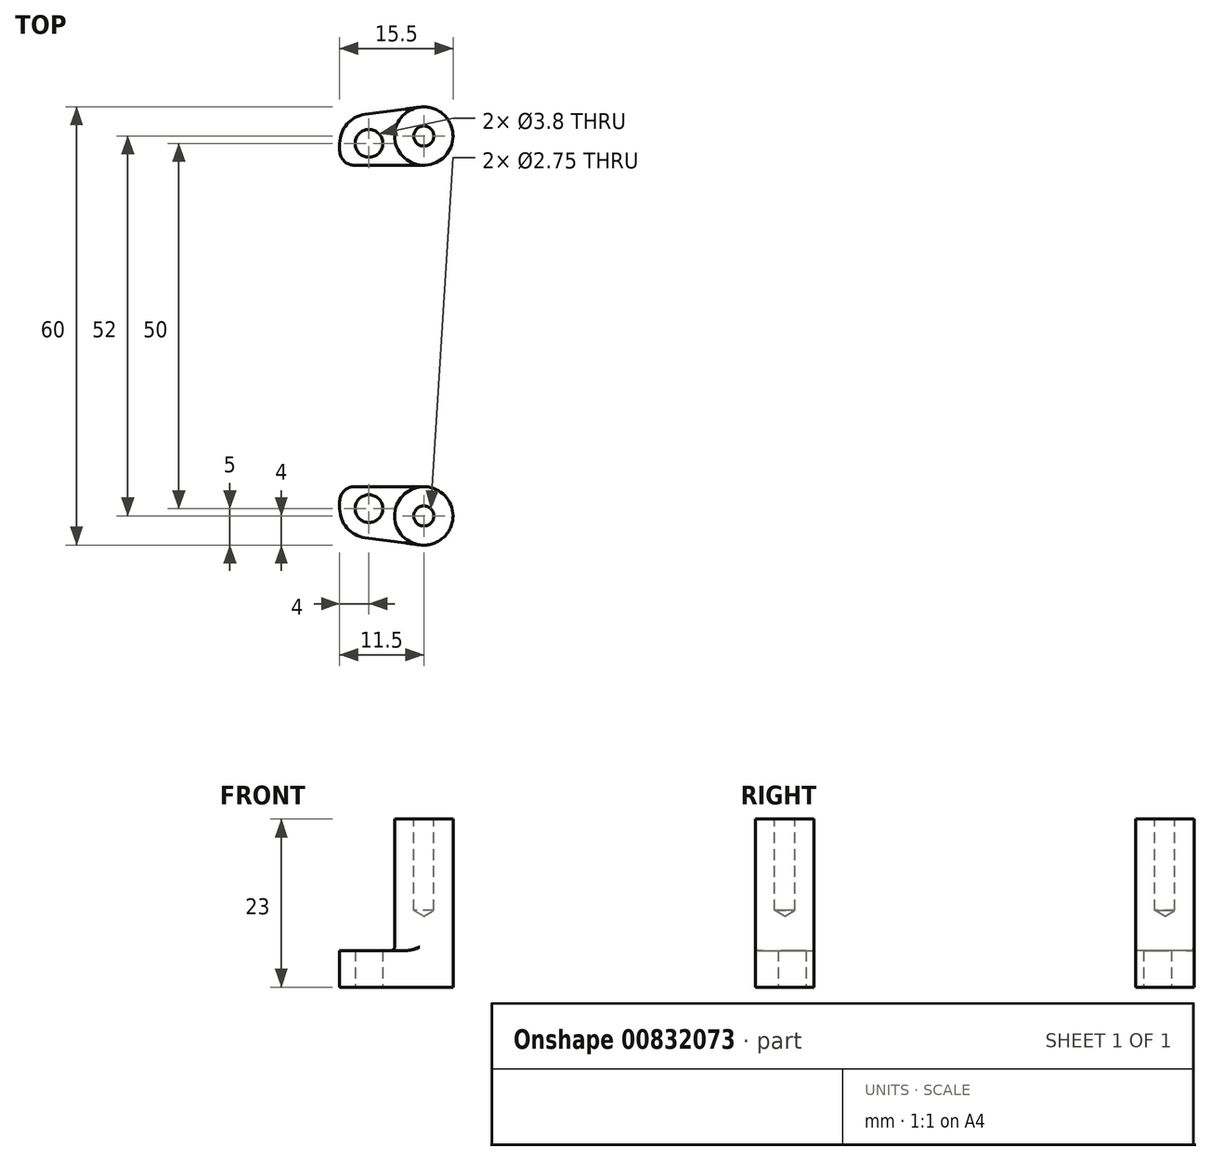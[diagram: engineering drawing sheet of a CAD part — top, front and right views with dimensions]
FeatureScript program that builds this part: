
annotation { "Feature Type Name" : "Feature", "Feature Type Description" : "" }
export const myFeature = defineFeature(function(context is Context, id is Id, definition is map)
    precondition{}
    {
        {
            var Q0;
            Q0=qCreatedBy(makeId("Top.planeOp"),FACE);
            var sketch = newSketch(context, id + "F0", { "sketchPlane" : qUnion([Q0])});
            skCircle(sketch, "E0", {"center": v(0, 0) * mm, "radius": 1.9 * mm});
            skLineSegment(sketch, "E1", {"start": v(7.5, -3) * mm, "end": v(-2, -3) * mm});
            skLineSegment(sketch, "E2", {"start": v(-4, -1) * mm, "end": v(-4, 0) * mm});
            skArc(sketch, "E3", {"start": v(-0.53, 3.96) * mm, "mid": v(-3, 2.63) * mm, "end": v(-4, 0) * mm});
            skLineSegment(sketch, "E4", {"start": v(-0.53, 3.96) * mm, "end": v(6.97, 4.96) * mm});
            skArc(sketch, "E5", {"start": v(7.5, -3) * mm, "mid": v(11.5, 1.26) * mm, "end": v(6.97, 4.96) * mm});
            skPoint(sketch, "E6.visualSharp", {"position": v(-4, -3) * mm});
            skArc(sketch, "E6.filletArc", {"start": v(-4, -1) * mm, "mid": v(-3.41, -2.41) * mm, "end": v(-2, -3) * mm});
            skSolve(sketch);
        }
        {
            var Q0;
            Q0 = qSketchRegion(id + "F0", true);
            extrude(context, id + "F1", {"entities" : qUnion([Q0]), "depth" : 23 * mm, "offsetDistance" : 25 * mm});
        }
        {
            var Q0;
            Q0=makeQuery(id+"F1.opExtrude","CAP_FACE",FACE,{"disambiguationData":[OSD([sQuery(id+"F0.wireOp",EDGE,"E0"),sQuery(id+"F0.wireOp",EDGE,"iPznz55F-rcXA-KLxn-qQNS-Mse66WEz7Yb1"),sQuery(id+"F0.wireOp",EDGE,"0pFobfdu-EYLJ-COly-NgAj-D3GZJxtIW0C9"),sQuery(id+"F0.wireOp",EDGE,"8qt3MjEX-NDzn-ihzM-cr2Q-z2v4d6qkCK1o"),sQuery(id+"F0.wireOp",EDGE,"E1")])],"isStart":false});
            var sketch = newSketch(context, id + "F2", { "sketchPlane" : qUnion([Q0])});
            skLineSegment(sketch, "E7.0.0", {"start": v(6.97, 4.96) * mm, "end": v(-0.53, 3.96) * mm});
            skArc(sketch, "E7.0.1", {"start": v(-0.53, 3.96) * mm, "mid": v(-3, 2.63) * mm, "end": v(-4, 0) * mm});
            skLineSegment(sketch, "E7.0.2", {"start": v(-4, 0) * mm, "end": v(-4, -1) * mm});
            skArc(sketch, "E7.0.3", {"start": v(-4, -1) * mm, "mid": v(-3.41, -2.41) * mm, "end": v(-2, -3) * mm});
            skLineSegment(sketch, "E7.0.4", {"start": v(-2, -3) * mm, "end": v(7.5, -3) * mm});
            skArc(sketch, "E8", {"start": v(6.97, 4.96) * mm, "mid": v(3.5, 0.74) * mm, "end": v(7.5, -3) * mm});
            skSolve(sketch);
        }
        {
            var Q0;
            Q0 = qSketchRegion(id + "F2", true);
            extrude(context, id + "F3", {"entities" : qUnion([Q0]), "operationType" : NewBodyOperationType.REMOVE, "oppositeDirection" : true, "depth" : 18 * mm, "offsetDistance" : 25 * mm});
        }
        {
            var Q0;
            Q0=makeQuery(id+"F3.boolean.opBoolean","COPY",EDGE,{"derivedFrom":makeQuery(id+"F3.opExtrude","CAP_EDGE",EDGE,{"disambiguationData":[OSD([sQuery(id+"F2.wireOp",EDGE,"E8")])],"isStart":false})});
            fillet(context, id + "F4", {"entities" : qUnion([Q0]), "radius" : 0.5 * mm, "tangentPropagation" : true, "allowEdgeOverflow" : false});
        }
        {
            var Q0;
            Q0=makeQuery(id+"F1.opExtrude","CAP_FACE",FACE,{"disambiguationData":[OSD([sQuery(id+"F0.wireOp",EDGE,"E0"),sQuery(id+"F0.wireOp",EDGE,"iPznz55F-rcXA-KLxn-qQNS-Mse66WEz7Yb1"),sQuery(id+"F0.wireOp",EDGE,"0pFobfdu-EYLJ-COly-NgAj-D3GZJxtIW0C9"),sQuery(id+"F0.wireOp",EDGE,"8qt3MjEX-NDzn-ihzM-cr2Q-z2v4d6qkCK1o"),sQuery(id+"F0.wireOp",EDGE,"E1")])],"isStart":false});
            var sketch = newSketch(context, id + "F5", { "sketchPlane" : qUnion([Q0])});
            skPoint(sketch, "E9", {"position": v(7.5, 1) * mm});
            skSolve(sketch);
        }
        {
            var Q0;
            Q0=sQuery(id+"F5.wireOp",VERTEX,"E9");
            var Q1;
            Q1=makeQuery(id+"F1.opExtrude","SWEPT_BODY",BODY,{"disambiguationData":[OSD([sQuery(id+"F0.wireOp",EDGE,"E0"),sQuery(id+"F0.wireOp",EDGE,"iPznz55F-rcXA-KLxn-qQNS-Mse66WEz7Yb1"),sQuery(id+"F0.wireOp",EDGE,"0pFobfdu-EYLJ-COly-NgAj-D3GZJxtIW0C9"),sQuery(id+"F0.wireOp",EDGE,"8qt3MjEX-NDzn-ihzM-cr2Q-z2v4d6qkCK1o"),sQuery(id+"F0.wireOp",EDGE,"E1")])]});
            hole(context, id + "F6", {"style" : HoleStyle.SIMPLE, "endStyle" : HoleEndStyle.BLIND, "holeDiameter" : 2.75 * mm, "majorDiameter" : 5 * mm, "holeDepth" : 12.5 * mm, "isTappedThrough" : true, "tappedDepth" : 12 * mm, "tapClearance" : 3, "locations" : qUnion([Q0]), "scope" : qUnion([Q1])});
        }
        {
            var Q0;
            Q0=qCreatedBy(makeId("Front.planeOp"),FACE);
            cPlane(context, id + "F7", {"entities" : qUnion([Q0]), "cplaneType" : CPlaneType.OFFSET, "offset" : 25 * mm, "width" : 150 * mm, "height" : 150 * mm});
        }
        {
            var Q0;
            Q0=makeQuery(id+"F1.opExtrude","SWEPT_BODY",BODY,{"disambiguationData":[OSD([sQuery(id+"F0.wireOp",EDGE,"E0"),sQuery(id+"F0.wireOp",EDGE,"E1"),sQuery(id+"F0.wireOp",EDGE,"E2"),sQuery(id+"F0.wireOp",EDGE,"E3"),sQuery(id+"F0.wireOp",EDGE,"E4"),sQuery(id+"F0.wireOp",EDGE,"E5"),sQuery(id+"F0.wireOp",EDGE,"E6.filletArc")])]});
            var Q1;
            Q1=qCreatedBy(id+"F7.planeOp",FACE);
            mirror(context, id + "F8", {"entities" : qUnion([Q0]), "mirrorPlane" : qUnion([Q1])});
        }
    });
